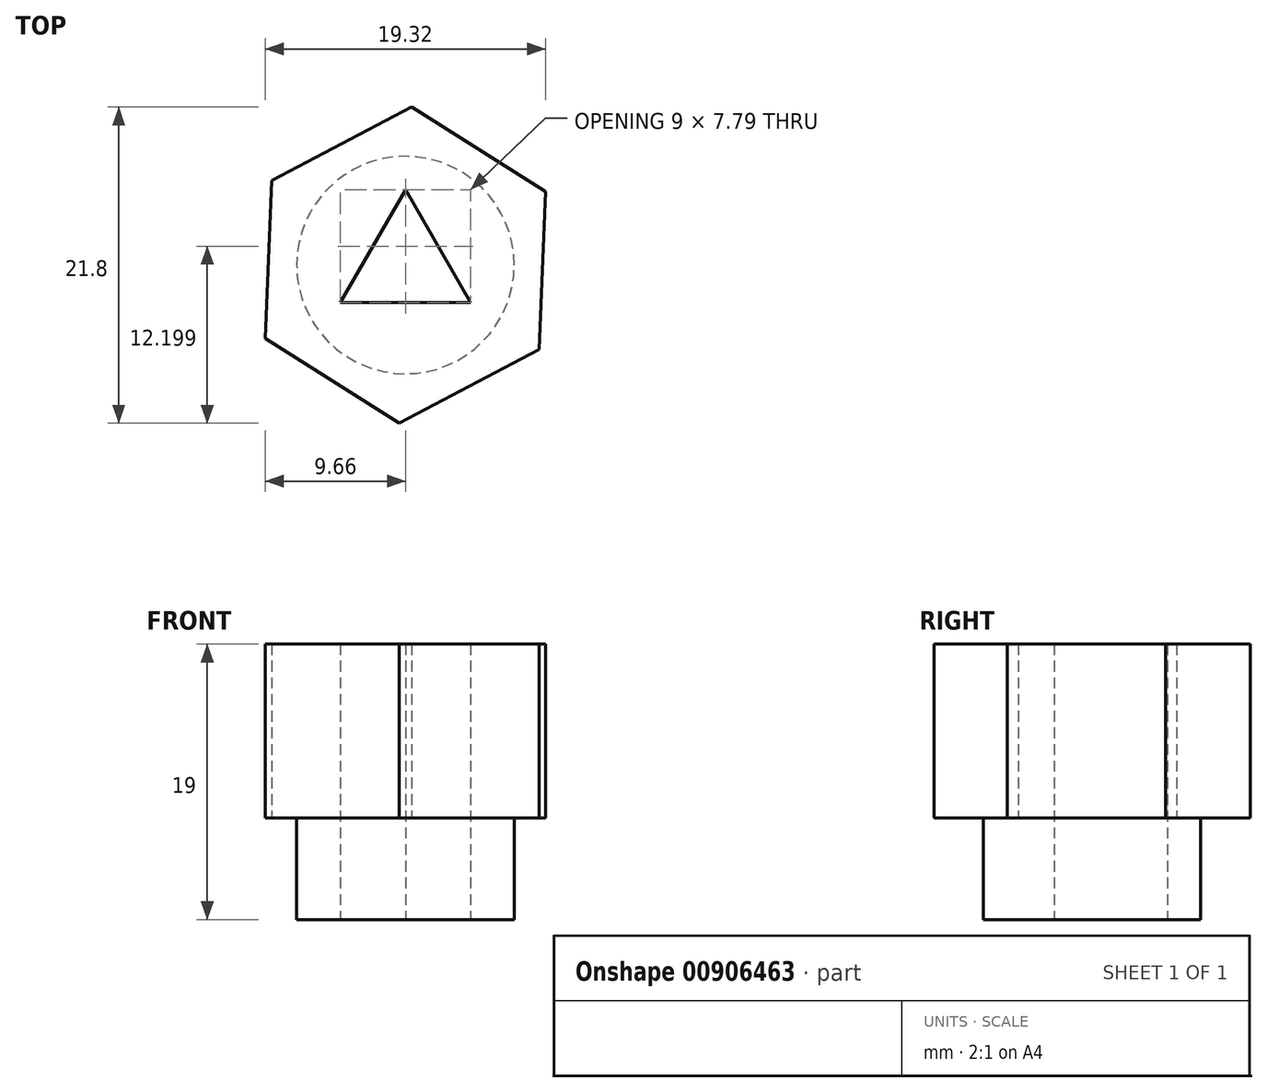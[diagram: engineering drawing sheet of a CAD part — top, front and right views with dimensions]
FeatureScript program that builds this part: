
annotation { "Feature Type Name" : "Feature", "Feature Type Description" : "" }
export const myFeature = defineFeature(function(context is Context, id is Id, definition is map)
    precondition{}
    {
        {
            var Q0;
            Q0=qCreatedBy(makeId("Top.planeOp"),FACE);
            var sketch = newSketch(context, id + "F0", { "sketchPlane" : qUnion([Q0])});
            skCircle(sketch, "E0", {"center": v(0, 0) * mm, "radius": 7.5 * mm});
            skLineSegment(sketch, "E1", {"start": v(0, 5.2) * mm, "end": v(-4.5, -2.6) * mm});
            skLineSegment(sketch, "E2", {"start": v(-4.5, -2.6) * mm, "end": v(4.5, -2.6) * mm});
            skLineSegment(sketch, "E3", {"start": v(4.5, -2.6) * mm, "end": v(0, 5.2) * mm});
            skLineSegment(sketch, "E4", {"start": v(0, 5.2) * mm, "end": v(0, 0) * mm, "construction": true});
            skLineSegment(sketch, "E5", {"start": v(0, 0) * mm, "end": v(-4.5, -2.6) * mm, "construction": true});
            skLineSegment(sketch, "E6", {"start": v(0, 0) * mm, "end": v(4.5, -2.6) * mm, "construction": true});
            skSolve(sketch);
        }
        {
            var Q0;
            Q0 = qSketchRegion(id + "F0", true);
            extrude(context, id + "F1", {"entities" : qUnion([Q0]), "depth" : 7 * mm, "offsetDistance" : 25 * mm});
        }
        {
            var Q0;
            Q0=makeQuery(id+"F1.opExtrude","CAP_FACE",FACE,{"disambiguationData":[OSD([sQuery(id+"F0.wireOp",EDGE,"E0"),sQuery(id+"F0.wireOp",EDGE,"E1"),sQuery(id+"F0.wireOp",EDGE,"E2"),sQuery(id+"F0.wireOp",EDGE,"E3")])],"isStart":false});
            var sketch = newSketch(context, id + "F2", { "sketchPlane" : qUnion([Q0])});
            skCircle(sketch, "E7.cCircle", {"center": v(0, 0) * mm, "radius": 9.45 * mm, "construction": true});
            skLineSegment(sketch, "E7.0", {"start": v(9.66, 5.07) * mm, "end": v(9.22, -5.83) * mm});
            skLineSegment(sketch, "E7.1", {"start": v(9.22, -5.83) * mm, "end": v(-0.44, -10.9) * mm});
            skLineSegment(sketch, "E7.2", {"start": v(-0.44, -10.9) * mm, "end": v(-9.66, -5.07) * mm});
            skLineSegment(sketch, "E7.3", {"start": v(-9.66, -5.07) * mm, "end": v(-9.22, 5.83) * mm});
            skLineSegment(sketch, "E7.4", {"start": v(-9.22, 5.83) * mm, "end": v(0.44, 10.9) * mm});
            skLineSegment(sketch, "E7.5", {"start": v(0.44, 10.9) * mm, "end": v(9.66, 5.07) * mm});
            skPoint(sketch, "E7.0.midPoint", {"position": v(9.44, -0.38) * mm});
            skSolve(sketch);
        }
        {
            var Q0;
            Q0=makeQuery(id+"F2.imprint","IMPRINT",FACE,{"disambiguationData":[TD([[makeQuery(id+"F2.imprint","IMPRINT",EDGE,{"derivedFrom":sQuery(id+"F2.wireOp",EDGE,"E7.0")}),-1.0]])]});
            var Q1;
            Q1=makeQuery(id+"F2.imprint","IMPRINT",FACE,{"disambiguationData":[TD([[makeQuery(id+"F2.imprint","IMPRINT",EDGE,{"derivedFrom":makeQuery(id+"F1.opExtrude","CAP_EDGE",EDGE,{"disambiguationData":[OSD([sQuery(id+"F0.wireOp",EDGE,"E0")])],"isStart":false})}),1.0]])]});
            extrude(context, id + "F3", {"entities" : qUnion([Q0, Q1]), "operationType" : NewBodyOperationType.ADD, "depth" : 12 * mm, "offsetDistance" : 25 * mm});
        }
    });
